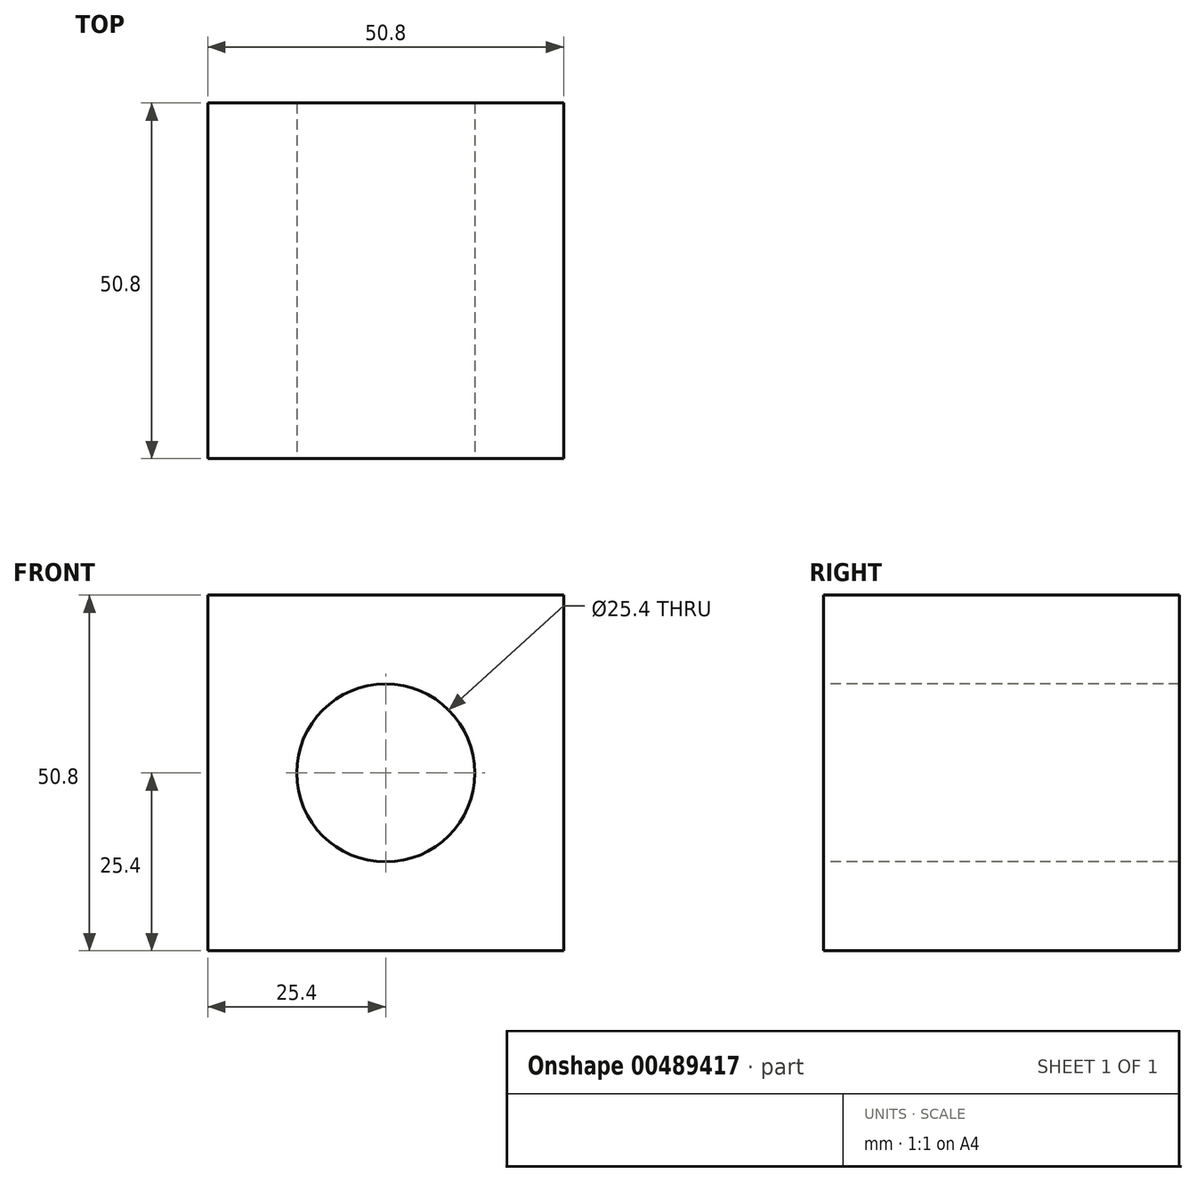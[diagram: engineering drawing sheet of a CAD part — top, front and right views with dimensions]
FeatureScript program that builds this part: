
annotation { "Feature Type Name" : "Feature", "Feature Type Description" : "" }
export const myFeature = defineFeature(function(context is Context, id is Id, definition is map)
    precondition{}
    {
        {
            var Q0;
            Q0=qCreatedBy(makeId("Front.planeOp"),FACE);
            var sketch = newSketch(context, id + "F0", { "sketchPlane" : qUnion([Q0])});
            skLineSegment(sketch, "E0", {"start": v(0, 0) * mm, "end": v(50.8, 0) * mm});
            skLineSegment(sketch, "E1", {"start": v(50.8, 0) * mm, "end": v(50.8, 50.8) * mm});
            skLineSegment(sketch, "E2", {"start": v(50.8, 50.8) * mm, "end": v(0, 50.8) * mm});
            skLineSegment(sketch, "E3", {"start": v(0, 50.8) * mm, "end": v(0, 0) * mm});
            skSolve(sketch);
        }
        {
            var Q0;
            Q0=makeQuery(id+"F0.imprint","IMPRINT",FACE,{"disambiguationData":[TD([[makeQuery(id+"F0.imprint","IMPRINT",EDGE,{"derivedFrom":sQuery(id+"F0.wireOp",EDGE,"E0")}),1.0]])]});
            extrude(context, id + "F1", {"entities" : qUnion([Q0]), "depth" : 50.8 * mm});
        }
        {
            var Q0;
            Q0=makeQuery(id+"F1.opExtrude","CAP_FACE",FACE,{"disambiguationData":[OSD([sQuery(id+"F0.wireOp",EDGE,"E0"),sQuery(id+"F0.wireOp",EDGE,"E1"),sQuery(id+"F0.wireOp",EDGE,"E2"),sQuery(id+"F0.wireOp",EDGE,"E3")])],"isStart":false});
            var sketch = newSketch(context, id + "F2", { "sketchPlane" : qUnion([Q0])});
            skPoint(sketch, "E4.center.orphan", {"position": v(25.4, 0) * mm});
            skCircle(sketch, "E5", {"center": v(25.4, 25.4) * mm, "radius": 12.7 * mm});
            skPoint(sketch, "E5.centerSnap0", {"position": v(50.8, 25.4) * mm});
            skSolve(sketch);
        }
        {
            var Q0;
            Q0=makeQuery(id+"F2.imprint","IMPRINT",FACE,{"disambiguationData":[TD([[makeQuery(id+"F2.imprint","IMPRINT",EDGE,{"derivedFrom":sQuery(id+"F2.wireOp",EDGE,"E5")}),1.0]])]});
            extrude(context, id + "F3", {"entities" : qUnion([Q0]), "operationType" : NewBodyOperationType.REMOVE, "oppositeDirection" : true, "depth" : 50.8 * mm});
        }
    });
